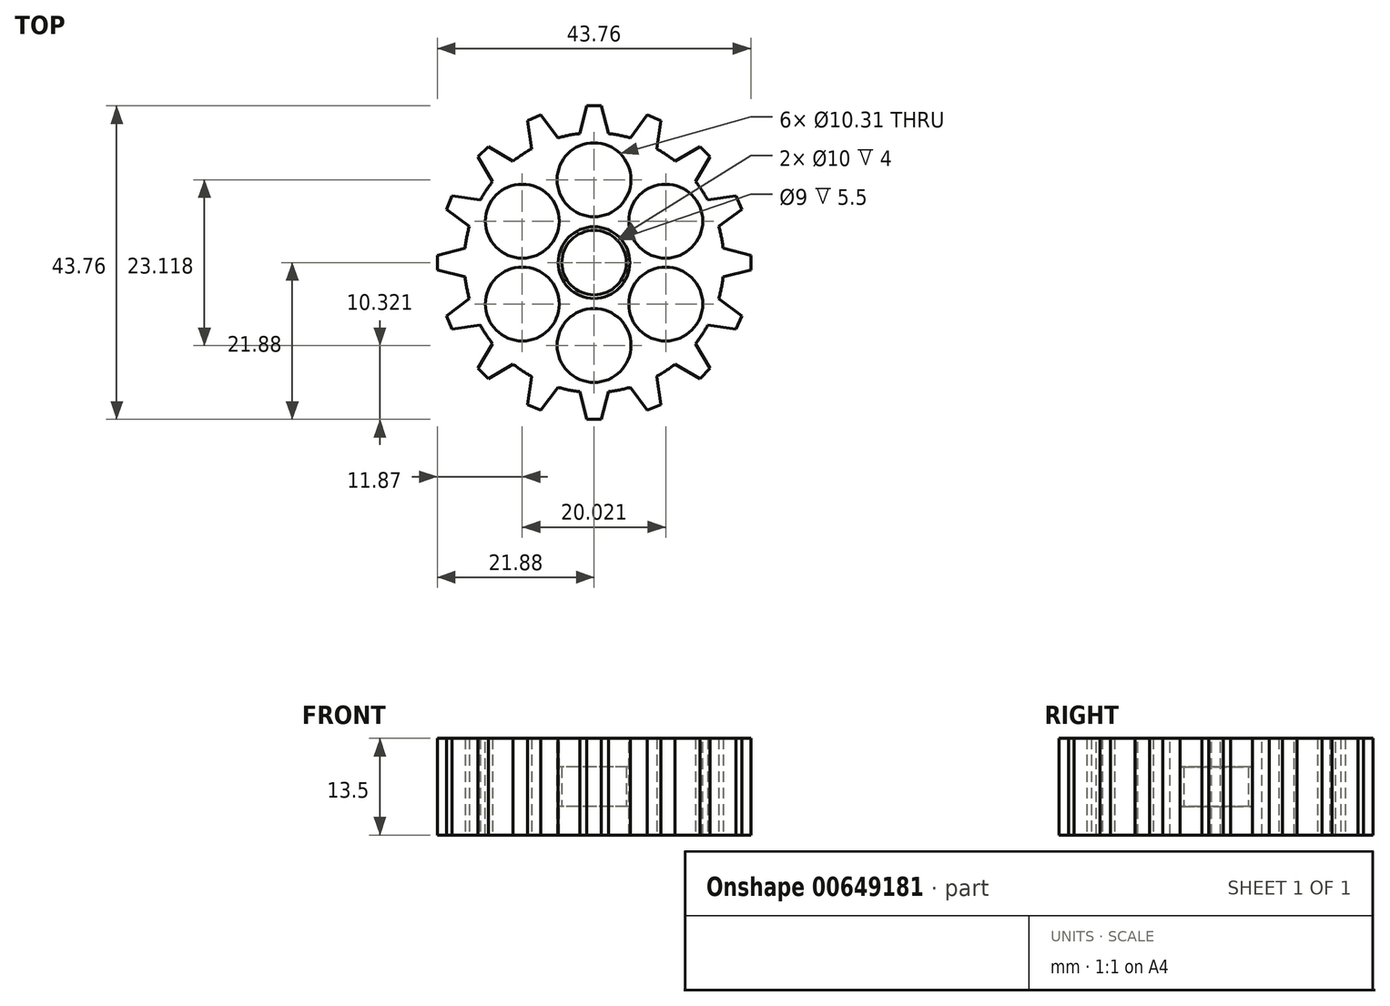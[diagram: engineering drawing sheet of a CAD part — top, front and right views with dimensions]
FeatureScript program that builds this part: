
annotation { "Feature Type Name" : "Feature", "Feature Type Description" : "" }
export const myFeature = defineFeature(function(context is Context, id is Id, definition is map)
    precondition{}
    {
        {
            var Q0;
            Q0=qCreatedBy(makeId("Top.planeOp"),FACE);
            var sketch = newSketch(context, id + "F0", { "sketchPlane" : qUnion([Q0])});
            skLineSegment(sketch, "E0", {"start": v(-18, -2) * mm, "end": v(-21.88, -1) * mm});
            skLineSegment(sketch, "E1", {"start": v(-21.88, -1) * mm, "end": v(-21.88, 1) * mm});
            skLineSegment(sketch, "E2", {"start": v(-21.88, 1) * mm, "end": v(-18, 2) * mm});
            skCircle(sketch, "E3", {"center": v(0, 0) * mm, "radius": 20 * mm, "construction": true});
            skPoint(sketch, "E4", {"position": v(-19.94, 1.5) * mm});
            skPoint(sketch, "E5", {"position": v(-19.94, -1.5) * mm});
            skArc(sketch, "E6", {"start": v(-17.4, 5.04) * mm, "mid": v(-17.77, 3.53) * mm, "end": v(-18, 2) * mm});
            skPoint(sketch, "E7", {"position": v(-21.88, 0) * mm});
            skLineSegment(sketch, "E8.1.0", {"start": v(-15.87, -8.74) * mm, "end": v(-19.83, -9.3) * mm});
            skLineSegment(sketch, "E8.1.1", {"start": v(-20.6, -7.45) * mm, "end": v(-17.4, -5.04) * mm});
            skArc(sketch, "E8.1.2", {"start": v(-18, -2) * mm, "mid": v(-17.77, -3.53) * mm, "end": v(-17.4, -5.04) * mm});
            skPoint(sketch, "E8.1.3", {"position": v(-19, -6.25) * mm});
            skPoint(sketch, "E8.1.4", {"position": v(-17.85, -9.02) * mm});
            skPoint(sketch, "E8.1.5", {"position": v(-20.21, -8.37) * mm});
            skLineSegment(sketch, "E8.1.6", {"start": v(-19.83, -9.3) * mm, "end": v(-20.6, -7.45) * mm});
            skLineSegment(sketch, "E8.2.0", {"start": v(-11.32, -14.15) * mm, "end": v(-14.76, -16.18) * mm});
            skLineSegment(sketch, "E8.2.1", {"start": v(-16.18, -14.76) * mm, "end": v(-14.15, -11.32) * mm});
            skArc(sketch, "E8.2.2", {"start": v(-15.87, -8.74) * mm, "mid": v(-15.06, -10.07) * mm, "end": v(-14.15, -11.32) * mm});
            skPoint(sketch, "E8.2.3", {"position": v(-15.16, -13.04) * mm});
            skPoint(sketch, "E8.2.4", {"position": v(-13.04, -15.16) * mm});
            skPoint(sketch, "E8.2.5", {"position": v(-15.47, -15.47) * mm});
            skLineSegment(sketch, "E8.2.6", {"start": v(-14.76, -16.18) * mm, "end": v(-16.18, -14.76) * mm});
            skLineSegment(sketch, "E8.3.0", {"start": v(-5.04, -17.4) * mm, "end": v(-7.45, -20.6) * mm});
            skLineSegment(sketch, "E8.3.1", {"start": v(-9.3, -19.83) * mm, "end": v(-8.74, -15.87) * mm});
            skArc(sketch, "E8.3.2", {"start": v(-11.32, -14.15) * mm, "mid": v(-10.07, -15.06) * mm, "end": v(-8.74, -15.87) * mm});
            skPoint(sketch, "E8.3.3", {"position": v(-9.02, -17.85) * mm});
            skPoint(sketch, "E8.3.4", {"position": v(-6.25, -19) * mm});
            skPoint(sketch, "E8.3.5", {"position": v(-8.37, -20.21) * mm});
            skLineSegment(sketch, "E8.3.6", {"start": v(-7.45, -20.6) * mm, "end": v(-9.3, -19.83) * mm});
            skLineSegment(sketch, "E8.4.0", {"start": v(2, -18) * mm, "end": v(1, -21.88) * mm});
            skLineSegment(sketch, "E8.4.1", {"start": v(-1, -21.88) * mm, "end": v(-2, -18) * mm});
            skArc(sketch, "E8.4.2", {"start": v(-5.04, -17.4) * mm, "mid": v(-3.53, -17.77) * mm, "end": v(-2, -18) * mm});
            skPoint(sketch, "E8.4.3", {"position": v(-1.5, -19.94) * mm});
            skPoint(sketch, "E8.4.4", {"position": v(1.5, -19.94) * mm});
            skPoint(sketch, "E8.4.5", {"position": v(0, -21.88) * mm});
            skLineSegment(sketch, "E8.4.6", {"start": v(1, -21.88) * mm, "end": v(-1, -21.88) * mm});
            skLineSegment(sketch, "E8.5.0", {"start": v(8.74, -15.87) * mm, "end": v(9.3, -19.83) * mm});
            skLineSegment(sketch, "E8.5.1", {"start": v(7.45, -20.6) * mm, "end": v(5.04, -17.4) * mm});
            skArc(sketch, "E8.5.2", {"start": v(2, -18) * mm, "mid": v(3.53, -17.77) * mm, "end": v(5.04, -17.4) * mm});
            skPoint(sketch, "E8.5.3", {"position": v(6.25, -19) * mm});
            skPoint(sketch, "E8.5.4", {"position": v(9.02, -17.85) * mm});
            skPoint(sketch, "E8.5.5", {"position": v(8.37, -20.21) * mm});
            skLineSegment(sketch, "E8.5.6", {"start": v(9.3, -19.83) * mm, "end": v(7.45, -20.6) * mm});
            skLineSegment(sketch, "E8.6.0", {"start": v(14.15, -11.32) * mm, "end": v(16.18, -14.76) * mm});
            skLineSegment(sketch, "E8.6.1", {"start": v(14.76, -16.18) * mm, "end": v(11.32, -14.15) * mm});
            skArc(sketch, "E8.6.2", {"start": v(8.74, -15.87) * mm, "mid": v(10.07, -15.06) * mm, "end": v(11.32, -14.15) * mm});
            skPoint(sketch, "E8.6.3", {"position": v(13.04, -15.16) * mm});
            skPoint(sketch, "E8.6.4", {"position": v(15.16, -13.04) * mm});
            skPoint(sketch, "E8.6.5", {"position": v(15.47, -15.47) * mm});
            skLineSegment(sketch, "E8.6.6", {"start": v(16.18, -14.76) * mm, "end": v(14.76, -16.18) * mm});
            skLineSegment(sketch, "E8.7.0", {"start": v(17.4, -5.04) * mm, "end": v(20.6, -7.45) * mm});
            skLineSegment(sketch, "E8.7.1", {"start": v(19.83, -9.3) * mm, "end": v(15.87, -8.74) * mm});
            skArc(sketch, "E8.7.2", {"start": v(14.15, -11.32) * mm, "mid": v(15.06, -10.07) * mm, "end": v(15.87, -8.74) * mm});
            skPoint(sketch, "E8.7.3", {"position": v(17.85, -9.02) * mm});
            skPoint(sketch, "E8.7.4", {"position": v(19, -6.25) * mm});
            skPoint(sketch, "E8.7.5", {"position": v(20.21, -8.37) * mm});
            skLineSegment(sketch, "E8.7.6", {"start": v(20.6, -7.45) * mm, "end": v(19.83, -9.3) * mm});
            skLineSegment(sketch, "E8.8.0", {"start": v(18, 2) * mm, "end": v(21.88, 1) * mm});
            skLineSegment(sketch, "E8.8.1", {"start": v(21.88, -1) * mm, "end": v(18, -2) * mm});
            skArc(sketch, "E8.8.2", {"start": v(17.4, -5.04) * mm, "mid": v(17.77, -3.53) * mm, "end": v(18, -2) * mm});
            skPoint(sketch, "E8.8.3", {"position": v(19.94, -1.5) * mm});
            skPoint(sketch, "E8.8.4", {"position": v(19.94, 1.5) * mm});
            skPoint(sketch, "E8.8.5", {"position": v(21.88, 0) * mm});
            skLineSegment(sketch, "E8.8.6", {"start": v(21.88, 1) * mm, "end": v(21.88, -1) * mm});
            skLineSegment(sketch, "E8.9.0", {"start": v(15.87, 8.74) * mm, "end": v(19.83, 9.3) * mm});
            skLineSegment(sketch, "E8.9.1", {"start": v(20.6, 7.45) * mm, "end": v(17.4, 5.04) * mm});
            skArc(sketch, "E8.9.2", {"start": v(18, 2) * mm, "mid": v(17.77, 3.53) * mm, "end": v(17.4, 5.04) * mm});
            skPoint(sketch, "E8.9.3", {"position": v(19, 6.25) * mm});
            skPoint(sketch, "E8.9.4", {"position": v(17.85, 9.02) * mm});
            skPoint(sketch, "E8.9.5", {"position": v(20.21, 8.37) * mm});
            skLineSegment(sketch, "E8.9.6", {"start": v(19.83, 9.3) * mm, "end": v(20.6, 7.45) * mm});
            skLineSegment(sketch, "E8.10.0", {"start": v(11.32, 14.15) * mm, "end": v(14.76, 16.18) * mm});
            skLineSegment(sketch, "E8.10.1", {"start": v(16.18, 14.76) * mm, "end": v(14.15, 11.32) * mm});
            skArc(sketch, "E8.10.2", {"start": v(15.87, 8.74) * mm, "mid": v(15.06, 10.07) * mm, "end": v(14.15, 11.32) * mm});
            skPoint(sketch, "E8.10.3", {"position": v(15.16, 13.04) * mm});
            skPoint(sketch, "E8.10.4", {"position": v(13.04, 15.16) * mm});
            skPoint(sketch, "E8.10.5", {"position": v(15.47, 15.47) * mm});
            skLineSegment(sketch, "E8.10.6", {"start": v(14.76, 16.18) * mm, "end": v(16.18, 14.76) * mm});
            skLineSegment(sketch, "E8.11.0", {"start": v(5.04, 17.4) * mm, "end": v(7.45, 20.6) * mm});
            skLineSegment(sketch, "E8.11.1", {"start": v(9.3, 19.83) * mm, "end": v(8.74, 15.87) * mm});
            skArc(sketch, "E8.11.2", {"start": v(11.32, 14.15) * mm, "mid": v(10.07, 15.06) * mm, "end": v(8.74, 15.87) * mm});
            skPoint(sketch, "E8.11.3", {"position": v(9.02, 17.85) * mm});
            skPoint(sketch, "E8.11.4", {"position": v(6.25, 19) * mm});
            skPoint(sketch, "E8.11.5", {"position": v(8.37, 20.21) * mm});
            skLineSegment(sketch, "E8.11.6", {"start": v(7.45, 20.6) * mm, "end": v(9.3, 19.83) * mm});
            skCircle(sketch, "E9", {"center": v(0, 0) * mm, "radius": 5 * mm});
            skCircle(sketch, "E10", {"center": v(0, 0) * mm, "radius": 4.5 * mm});
            skLineSegment(sketch, "E11.2.12.0", {"start": v(-2, 18) * mm, "end": v(-1, 21.88) * mm});
            skLineSegment(sketch, "E11.3.12.0", {"start": v(1, 21.88) * mm, "end": v(2, 18) * mm});
            skArc(sketch, "E11.6.12.0", {"start": v(5.04, 17.4) * mm, "mid": v(3.53, 17.77) * mm, "end": v(2, 18) * mm});
            skPoint(sketch, "E11.10.12.0", {"position": v(1.5, 19.94) * mm});
            skPoint(sketch, "E11.11.12.0", {"position": v(-1.5, 19.94) * mm});
            skPoint(sketch, "E11.12.12.0", {"position": v(0, 21.88) * mm});
            skLineSegment(sketch, "E11.13.12.0", {"start": v(-1, 21.88) * mm, "end": v(1, 21.88) * mm});
            skLineSegment(sketch, "E11.2.13.0", {"start": v(-8.74, 15.87) * mm, "end": v(-9.3, 19.83) * mm});
            skLineSegment(sketch, "E11.3.13.0", {"start": v(-7.45, 20.6) * mm, "end": v(-5.04, 17.4) * mm});
            skArc(sketch, "E11.6.13.0", {"start": v(-2, 18) * mm, "mid": v(-3.53, 17.77) * mm, "end": v(-5.04, 17.4) * mm});
            skPoint(sketch, "E11.10.13.0", {"position": v(-6.25, 19) * mm});
            skPoint(sketch, "E11.11.13.0", {"position": v(-9.02, 17.85) * mm});
            skPoint(sketch, "E11.12.13.0", {"position": v(-8.37, 20.21) * mm});
            skLineSegment(sketch, "E11.13.13.0", {"start": v(-9.3, 19.83) * mm, "end": v(-7.45, 20.6) * mm});
            skLineSegment(sketch, "E11.2.14.0", {"start": v(-14.15, 11.32) * mm, "end": v(-16.18, 14.76) * mm});
            skLineSegment(sketch, "E11.3.14.0", {"start": v(-14.76, 16.18) * mm, "end": v(-11.32, 14.15) * mm});
            skArc(sketch, "E11.6.14.0", {"start": v(-8.74, 15.87) * mm, "mid": v(-10.07, 15.06) * mm, "end": v(-11.32, 14.15) * mm});
            skPoint(sketch, "E11.10.14.0", {"position": v(-13.04, 15.16) * mm});
            skPoint(sketch, "E11.11.14.0", {"position": v(-15.16, 13.04) * mm});
            skPoint(sketch, "E11.12.14.0", {"position": v(-15.47, 15.47) * mm});
            skLineSegment(sketch, "E11.13.14.0", {"start": v(-16.18, 14.76) * mm, "end": v(-14.76, 16.18) * mm});
            skLineSegment(sketch, "E11.2.15.0", {"start": v(-17.4, 5.04) * mm, "end": v(-20.6, 7.45) * mm});
            skLineSegment(sketch, "E11.3.15.0", {"start": v(-19.83, 9.3) * mm, "end": v(-15.87, 8.74) * mm});
            skArc(sketch, "E11.6.15.0", {"start": v(-14.15, 11.32) * mm, "mid": v(-15.06, 10.07) * mm, "end": v(-15.87, 8.74) * mm});
            skPoint(sketch, "E11.10.15.0", {"position": v(-17.85, 9.02) * mm});
            skPoint(sketch, "E11.11.15.0", {"position": v(-19, 6.25) * mm});
            skPoint(sketch, "E11.12.15.0", {"position": v(-20.21, 8.37) * mm});
            skLineSegment(sketch, "E11.13.15.0", {"start": v(-20.6, 7.45) * mm, "end": v(-19.83, 9.3) * mm});
            skSolve(sketch);
        }
        {
            var Q0;
            Q0=qSketchRegion(id+"F0",true);
            extrude(context, id + "F1", {"entities" : qUnion([Q0]), "endBound" : BoundingType.SYMMETRIC, "depth" : 13.5 * mm});
        }
        {
            var Q0;
            Q0=makeQuery(id+"F0.imprint","IMPRINT",FACE,{"disambiguationData":[TD([[makeQuery(id+"F0.imprint","IMPRINT",EDGE,{"derivedFrom":sQuery(id+"F0.wireOp",EDGE,"E9")}),1.0]])]});
            extrude(context, id + "F2", {"entities" : qUnion([Q0]), "operationType" : NewBodyOperationType.ADD, "endBound" : BoundingType.SYMMETRIC, "depth" : 5.5 * mm});
        }
        {
            var Q0;
            Q0=makeQuery(id+"F1.opExtrude","CAP_FACE",FACE,{"disambiguationData":[OSD([sQuery(id+"F0.wireOp",EDGE,"E0"),sQuery(id+"F0.wireOp",EDGE,"E1"),sQuery(id+"F0.wireOp",EDGE,"E2"),sQuery(id+"F0.wireOp",EDGE,"E6"),sQuery(id+"F0.wireOp",EDGE,"E8.1.0"),sQuery(id+"F0.wireOp",EDGE,"E8.1.1"),sQuery(id+"F0.wireOp",EDGE,"E8.1.2"),sQuery(id+"F0.wireOp",EDGE,"E8.1.6"),sQuery(id+"F0.wireOp",EDGE,"E8.2.0"),sQuery(id+"F0.wireOp",EDGE,"E8.2.1"),sQuery(id+"F0.wireOp",EDGE,"E8.2.2"),sQuery(id+"F0.wireOp",EDGE,"E8.2.6"),sQuery(id+"F0.wireOp",EDGE,"E8.3.0"),sQuery(id+"F0.wireOp",EDGE,"E8.3.1"),sQuery(id+"F0.wireOp",EDGE,"E8.3.2"),sQuery(id+"F0.wireOp",EDGE,"E8.3.6"),sQuery(id+"F0.wireOp",EDGE,"E8.4.0"),sQuery(id+"F0.wireOp",EDGE,"E8.4.1"),sQuery(id+"F0.wireOp",EDGE,"E8.4.2"),sQuery(id+"F0.wireOp",EDGE,"E8.4.6"),sQuery(id+"F0.wireOp",EDGE,"E8.5.0"),sQuery(id+"F0.wireOp",EDGE,"E8.5.1"),sQuery(id+"F0.wireOp",EDGE,"E8.5.2"),sQuery(id+"F0.wireOp",EDGE,"E8.5.6"),sQuery(id+"F0.wireOp",EDGE,"E8.6.0"),sQuery(id+"F0.wireOp",EDGE,"E8.6.1"),sQuery(id+"F0.wireOp",EDGE,"E8.6.2"),sQuery(id+"F0.wireOp",EDGE,"E8.6.6"),sQuery(id+"F0.wireOp",EDGE,"E8.7.0"),sQuery(id+"F0.wireOp",EDGE,"E8.7.1"),sQuery(id+"F0.wireOp",EDGE,"E8.7.2"),sQuery(id+"F0.wireOp",EDGE,"E8.7.6"),sQuery(id+"F0.wireOp",EDGE,"E8.8.0"),sQuery(id+"F0.wireOp",EDGE,"E8.8.1"),sQuery(id+"F0.wireOp",EDGE,"E8.8.2"),sQuery(id+"F0.wireOp",EDGE,"E8.8.6"),sQuery(id+"F0.wireOp",EDGE,"E8.9.0"),sQuery(id+"F0.wireOp",EDGE,"E8.9.1"),sQuery(id+"F0.wireOp",EDGE,"E8.9.2"),sQuery(id+"F0.wireOp",EDGE,"E8.9.6"),sQuery(id+"F0.wireOp",EDGE,"E8.10.0"),sQuery(id+"F0.wireOp",EDGE,"E8.10.1"),sQuery(id+"F0.wireOp",EDGE,"E8.10.2"),sQuery(id+"F0.wireOp",EDGE,"E8.10.6"),sQuery(id+"F0.wireOp",EDGE,"E8.11.0"),sQuery(id+"F0.wireOp",EDGE,"E8.11.1"),sQuery(id+"F0.wireOp",EDGE,"E8.11.2"),sQuery(id+"F0.wireOp",EDGE,"E8.11.6"),sQuery(id+"F0.wireOp",EDGE,"E9")])],"isStart":false});
            var sketch = newSketch(context, id + "F3", { "sketchPlane" : qUnion([Q0])});
            skCircle(sketch, "E12", {"center": v(0, 11.56) * mm, "radius": 5.15 * mm});
            skLineSegment(sketch, "E13", {"start": v(0, 5) * mm, "end": v(0, 18.12) * mm, "construction": true});
            skArc(sketch, "E14", {"start": v(17.4, 5.04) * mm, "mid": v(16.74, 6.93) * mm, "end": v(15.87, 8.74) * mm, "construction": true});
            skLineSegment(sketch, "E15.1.0", {"start": v(-4.33, 2.5) * mm, "end": v(-15.7, 9.06) * mm, "construction": true});
            skCircle(sketch, "E15.1.1", {"center": v(-10.01, 5.78) * mm, "radius": 5.15 * mm});
            skArc(sketch, "E15.1.2", {"start": v(4.33, 17.6) * mm, "mid": v(2.36, 17.96) * mm, "end": v(0.37, 18.11) * mm, "construction": true});
            skLineSegment(sketch, "E15.2.0", {"start": v(-4.33, -2.5) * mm, "end": v(-15.7, -9.06) * mm, "construction": true});
            skCircle(sketch, "E15.2.1", {"center": v(-10.01, -5.78) * mm, "radius": 5.15 * mm});
            skArc(sketch, "E15.2.2", {"start": v(-13.07, 12.55) * mm, "mid": v(-14.37, 11.03) * mm, "end": v(-15.5, 9.38) * mm, "construction": true});
            skLineSegment(sketch, "E16.1.3.0", {"start": v(0, -5) * mm, "end": v(0, -18.12) * mm, "construction": true});
            skCircle(sketch, "E16.3.3.0", {"center": v(0, -11.56) * mm, "radius": 5.15 * mm});
            skArc(sketch, "E16.5.3.0", {"start": v(-17.4, -5.04) * mm, "mid": v(-16.74, -6.93) * mm, "end": v(-15.87, -8.74) * mm, "construction": true});
            skLineSegment(sketch, "E16.1.4.0", {"start": v(4.33, -2.5) * mm, "end": v(15.7, -9.06) * mm, "construction": true});
            skCircle(sketch, "E16.3.4.0", {"center": v(10.01, -5.78) * mm, "radius": 5.15 * mm});
            skArc(sketch, "E16.5.4.0", {"start": v(-4.33, -17.6) * mm, "mid": v(-2.36, -17.96) * mm, "end": v(-0.37, -18.11) * mm, "construction": true});
            skLineSegment(sketch, "E16.1.5.0", {"start": v(4.33, 2.5) * mm, "end": v(15.7, 9.06) * mm, "construction": true});
            skCircle(sketch, "E16.3.5.0", {"center": v(10.01, 5.78) * mm, "radius": 5.15 * mm});
            skArc(sketch, "E16.5.5.0", {"start": v(13.07, -12.55) * mm, "mid": v(14.37, -11.03) * mm, "end": v(15.5, -9.38) * mm, "construction": true});
            skSolve(sketch);
        }
        {
            var Q0;
            Q0=qSketchRegion(id+"F3",true);
            extrude(context, id + "F4", {"entities" : qUnion([Q0]), "operationType" : NewBodyOperationType.REMOVE, "endBound" : BoundingType.THROUGH_ALL, "oppositeDirection" : true, "depth" : 25 * mm});
        }
    });
